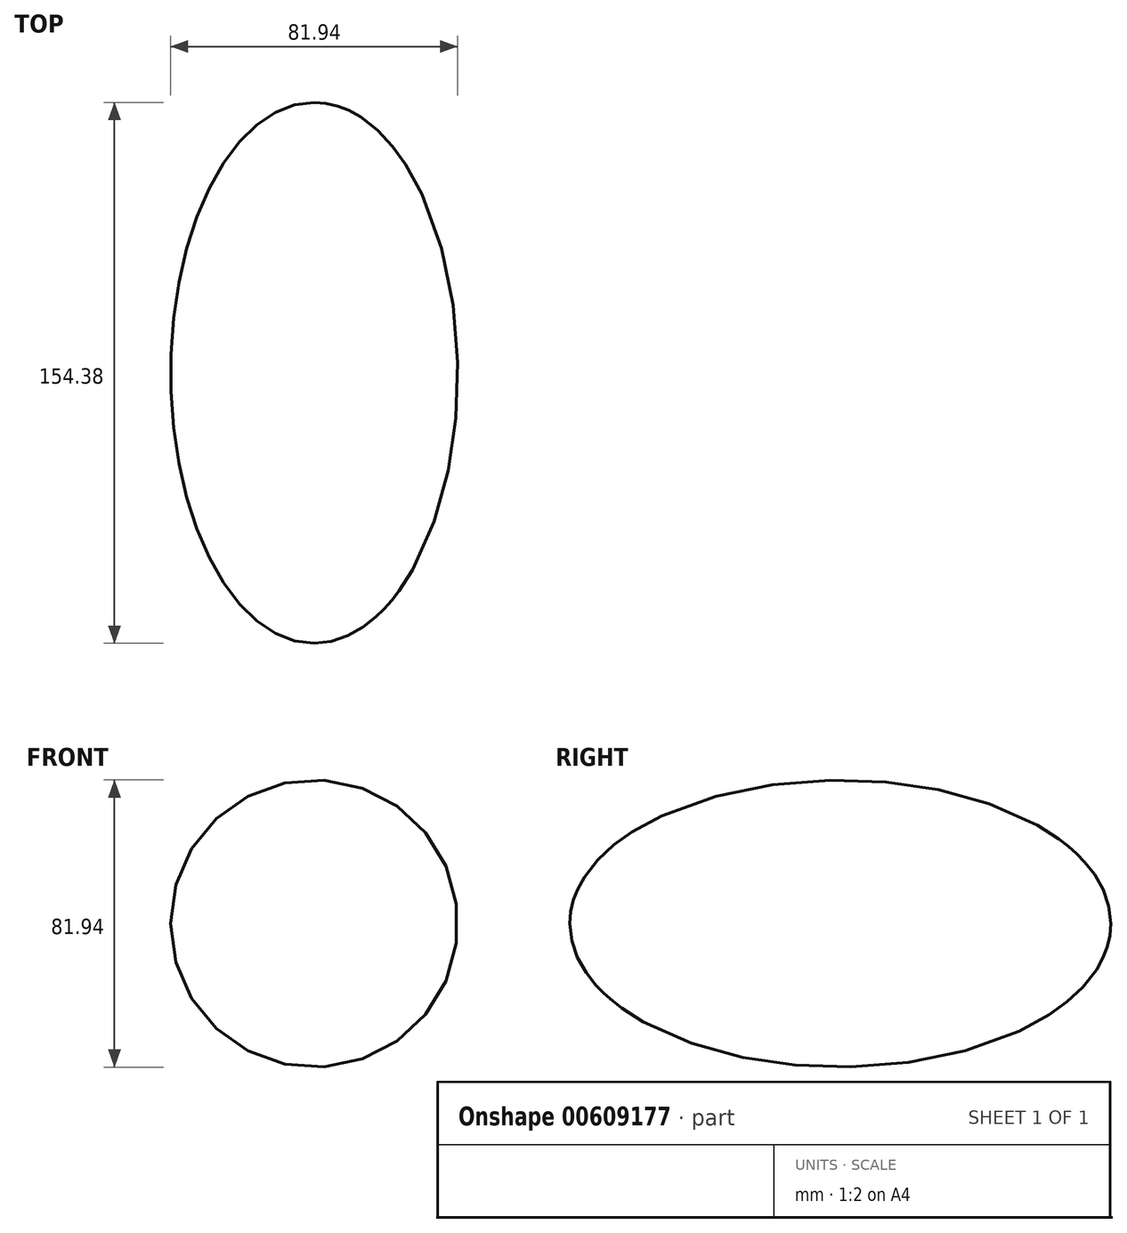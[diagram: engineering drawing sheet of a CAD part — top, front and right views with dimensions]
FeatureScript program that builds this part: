
annotation { "Feature Type Name" : "Feature", "Feature Type Description" : "" }
export const myFeature = defineFeature(function(context is Context, id is Id, definition is map)
    precondition{}
    {
        {
            var Q0;
            Q0=qCreatedBy(makeId("Top.planeOp"),FACE);
            var sketch = newSketch(context, id + "F0", { "sketchPlane" : qUnion([Q0])});
            skEllipticalArc(sketch, "E0", {});
            skLineSegment(sketch, "E1", {"start": v(0, 77.2) * mm, "end": v(0, -77.2) * mm});
            const initialGuessF0  = {"E0": [0, 0, 0, 1, 0.07719380408525467, 0.040971662386725755, 0, 3.141592653589793]};
            skSetInitialGuess(sketch, initialGuessF0);
            skSolve(sketch);
        }
        {
            var Q0;
            Q0=makeQuery(id+"F0.imprint","IMPRINT",FACE,{"disambiguationData":[TD([[makeQuery(id+"F0.imprint","IMPRINT",EDGE,{"derivedFrom":sQuery(id+"F0.wireOp",EDGE,"E0")}),1.0]])]});
            var Q1;
            Q1=sQuery(id+"F0.wireOp",EDGE,"E1");
            revolve(context, id + "F1", {"entities" : qUnion([Q0]), "axis" : qUnion([Q1]), "revolveType" : RevolveType.FULL});
        }
    });
